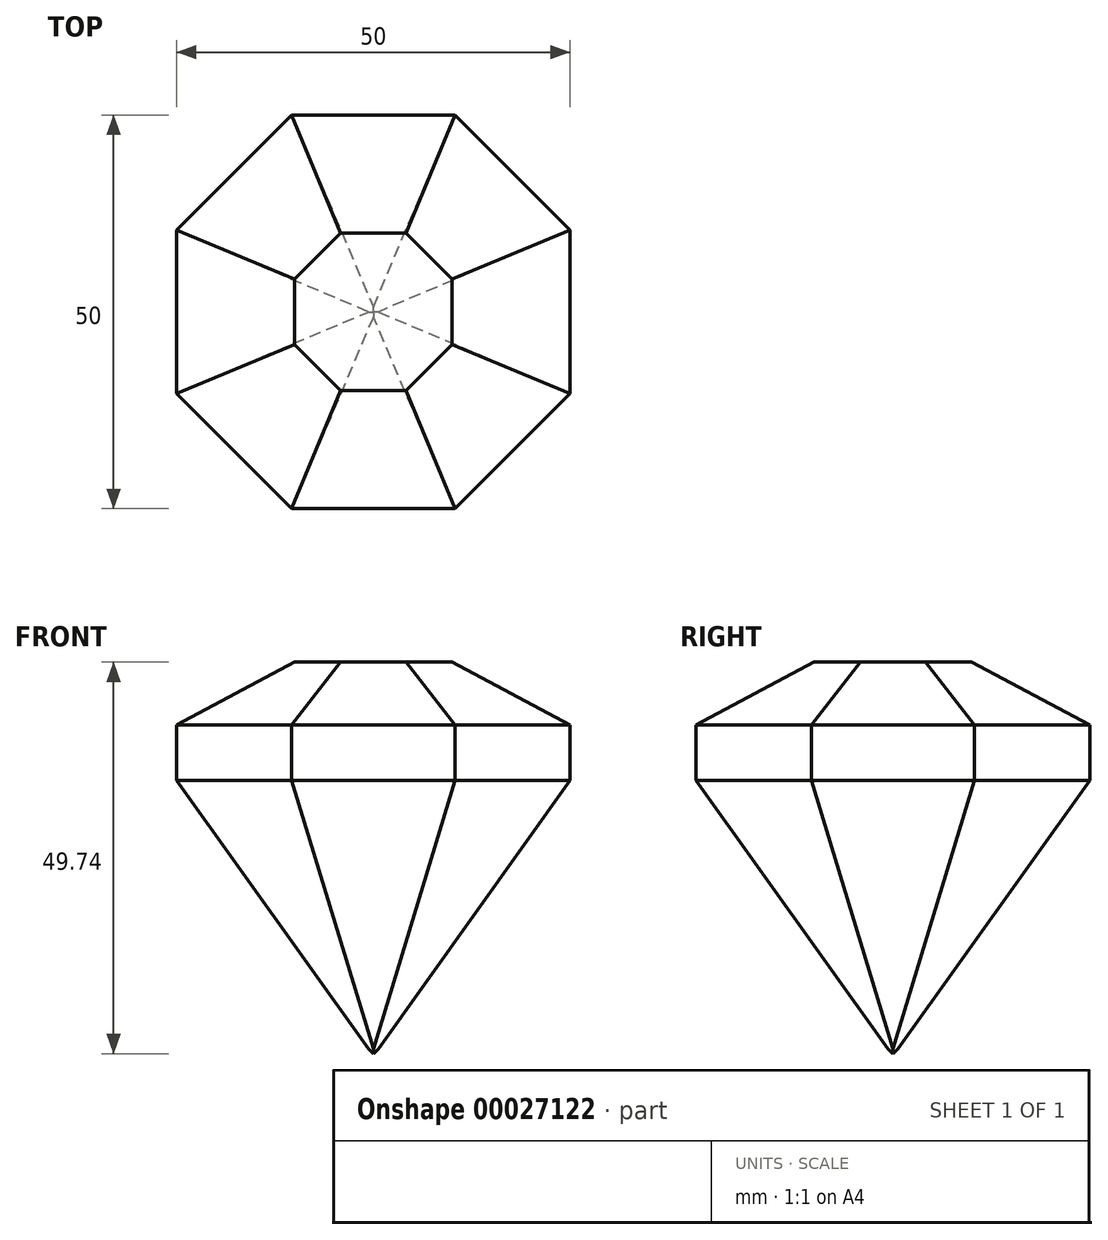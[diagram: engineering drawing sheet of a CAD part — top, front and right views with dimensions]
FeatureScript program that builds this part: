
annotation { "Feature Type Name" : "Feature", "Feature Type Description" : "" }
export const myFeature = defineFeature(function(context is Context, id is Id, definition is map)
    precondition{}
    {
        {
            var Q0;
            Q0=qCreatedBy(makeId("Front.planeOp"),FACE);
            var sketch = newSketch(context, id + "F0", { "sketchPlane" : qUnion([Q0])});
            skLineSegment(sketch, "E0.bottom", {"start": v(0, 0) * mm, "end": v(50, 0) * mm});
            skLineSegment(sketch, "E0.top", {"start": v(0, -50) * mm, "end": v(50, -50) * mm});
            skLineSegment(sketch, "E0.left", {"start": v(0, 0) * mm, "end": v(0, -50) * mm});
            skLineSegment(sketch, "E0.right", {"start": v(50, 0) * mm, "end": v(50, -50) * mm});
            skSolve(sketch);
        }
        {
            var Q0;
            Q0=makeQuery(id+"F0.imprint","IMPRINT",FACE,{"disambiguationData":[TD([[makeQuery(id+"F0.imprint","IMPRINT",EDGE,{"derivedFrom":sQuery(id+"F0.wireOp",EDGE,"E0.bottom")}),-1.0]])]});
            extrude(context, id + "F1", {"entities" : qUnion([Q0]), "depth" : 50 * mm});
        }
        {
            var Q0;
            Q0=makeQuery(id+"F1.opExtrude","CAP_EDGE",EDGE,{"disambiguationData":[OSD([sQuery(id+"F0.wireOp",EDGE,"E0.right")])],"isStart":false});
            cPlane(context, id + "F2", {"entities" : qUnion([Q0]), "cplaneType" : CPlaneType.LINE_ANGLE, "offset" : 150 * mm, "angle" : 45 * degree, "width" : 150 * mm, "height" : 150 * mm});
        }
        {
            var Q0;
            Q0=makeQuery(id+"F1.opExtrude","CAP_EDGE",EDGE,{"disambiguationData":[OSD([sQuery(id+"F0.wireOp",EDGE,"E0.left")])],"isStart":false});
            cPlane(context, id + "F3", {"entities" : qUnion([Q0]), "cplaneType" : CPlaneType.LINE_ANGLE, "offset" : 0 * mm, "angle" : 135 * degree, "width" : 150 * mm, "height" : 150 * mm});
        }
        {
            var Q0;
            Q0=makeQuery(id+"F1.opExtrude","CAP_FACE",FACE,{"disambiguationData":[OSD([sQuery(id+"F0.wireOp",EDGE,"E0.bottom"),sQuery(id+"F0.wireOp",EDGE,"E0.top"),sQuery(id+"F0.wireOp",EDGE,"E0.left"),sQuery(id+"F0.wireOp",EDGE,"E0.right")])],"isStart":false});
            var sketch = newSketch(context, id + "F4", { "sketchPlane" : qUnion([Q0])});
            skLineSegment(sketch, "E1", {"start": v(25, 0) * mm, "end": v(25, -50) * mm});
            skLineSegment(sketch, "E2", {"start": v(25, -50) * mm, "end": v(0, -15) * mm});
            skLineSegment(sketch, "E3", {"start": v(0, -15) * mm, "end": v(0, -8) * mm});
            skLineSegment(sketch, "E4", {"start": v(0, -8) * mm, "end": v(15, 0) * mm});
            skLineSegment(sketch, "E5", {"start": v(15, 0) * mm, "end": v(35, 0) * mm});
            skLineSegment(sketch, "E6", {"start": v(35, 0) * mm, "end": v(50, -8) * mm});
            skLineSegment(sketch, "E7", {"start": v(50, -8) * mm, "end": v(50, -15) * mm});
            skLineSegment(sketch, "E8", {"start": v(50, -15) * mm, "end": v(25, -50) * mm});
            skSolve(sketch);
        }
        {
            var Q0;
            {var subQ1=sQuery(id+"F4.wireOp",EDGE,"E4");Q0=makeQuery(id+"F4.imprint","IMPRINT",FACE,{"disambiguationData":[TD([[makeQuery(id+"F4.imprint","IMPRINT",EDGE,{"derivedFrom":subQ1}),1.0]])]});}
            var Q1;
            {var subQ1=sQuery(id+"F4.wireOp",EDGE,"E6");Q1=makeQuery(id+"F4.imprint","IMPRINT",FACE,{"disambiguationData":[TD([[makeQuery(id+"F4.imprint","IMPRINT",EDGE,{"derivedFrom":subQ1}),1.0]])]});}
            var Q2;
            {var subQ1=sQuery(id+"F4.wireOp",EDGE,"E8");Q2=makeQuery(id+"F4.imprint","IMPRINT",FACE,{"disambiguationData":[TD([[makeQuery(id+"F4.imprint","IMPRINT",EDGE,{"derivedFrom":subQ1}),1.0]])]});}
            var Q3;
            {var subQ1=sQuery(id+"F4.wireOp",EDGE,"E2");Q3=makeQuery(id+"F4.imprint","IMPRINT",FACE,{"disambiguationData":[TD([[makeQuery(id+"F4.imprint","IMPRINT",EDGE,{"derivedFrom":subQ1}),1.0]])]});}
            extrude(context, id + "F5", {"entities" : qUnion([Q0, Q1, Q2, Q3]), "operationType" : NewBodyOperationType.REMOVE, "endBound" : BoundingType.THROUGH_ALL, "oppositeDirection" : true, "depth" : 25 * mm});
        }
        {
            var Q0;
            Q0=makeQuery(id+"F1.opExtrude","SWEPT_FACE",FACE,{"disambiguationData":[OSD([sQuery(id+"F0.wireOp",EDGE,"E0.right")])]});
            var sketch = newSketch(context, id + "F6", { "sketchPlane" : qUnion([Q0])});
            skLineSegment(sketch, "E9", {"start": v(-25, 0) * mm, "end": v(-25, -50) * mm});
            skLineSegment(sketch, "E10", {"start": v(-25, -50) * mm, "end": v(-50, -15) * mm});
            skLineSegment(sketch, "E11", {"start": v(-50, -15) * mm, "end": v(-50, -8) * mm});
            skLineSegment(sketch, "E12", {"start": v(-50, -8) * mm, "end": v(-35, 0) * mm});
            skLineSegment(sketch, "E13", {"start": v(-35, 0) * mm, "end": v(-15, 0) * mm});
            skLineSegment(sketch, "E14", {"start": v(-15, 0) * mm, "end": v(0, -8) * mm});
            skLineSegment(sketch, "E15", {"start": v(0, -8) * mm, "end": v(0, -15) * mm});
            skLineSegment(sketch, "E16", {"start": v(0, -15) * mm, "end": v(-25, -50) * mm});
            skLineSegment(sketch, "E17.bottom", {"start": v(0, 0) * mm, "end": v(-50, 0) * mm});
            skLineSegment(sketch, "E17.top", {"start": v(0, -50) * mm, "end": v(-50, -50) * mm});
            skLineSegment(sketch, "E17.left", {"start": v(0, 0) * mm, "end": v(0, -50) * mm});
            skLineSegment(sketch, "E17.right", {"start": v(-50, 0) * mm, "end": v(-50, -50) * mm});
            skSolve(sketch);
        }
        {
            var Q0;
            {var subQ3=sQuery(id+"F6.wireOp",EDGE,"E12");Q0=makeQuery(id+"F6.imprint","IMPRINT",FACE,{"disambiguationData":[TD([[makeQuery(id+"F6.imprint","IMPRINT",EDGE,{"derivedFrom":subQ3}),1.0]])]});}
            var Q1;
            {var subQ3=sQuery(id+"F6.wireOp",EDGE,"E14");Q1=makeQuery(id+"F6.imprint","IMPRINT",FACE,{"disambiguationData":[TD([[makeQuery(id+"F6.imprint","IMPRINT",EDGE,{"derivedFrom":subQ3}),1.0]])]});}
            var Q2;
            {var subQ3=sQuery(id+"F6.wireOp",EDGE,"E16");Q2=makeQuery(id+"F6.imprint","IMPRINT",FACE,{"disambiguationData":[TD([[makeQuery(id+"F6.imprint","IMPRINT",EDGE,{"derivedFrom":subQ3}),1.0]])]});}
            var Q3;
            {var subQ3=sQuery(id+"F6.wireOp",EDGE,"E10");Q3=makeQuery(id+"F6.imprint","IMPRINT",FACE,{"disambiguationData":[TD([[makeQuery(id+"F6.imprint","IMPRINT",EDGE,{"derivedFrom":subQ3}),1.0]])]});}
            extrude(context, id + "F7", {"entities" : qUnion([Q0, Q1, Q2, Q3]), "operationType" : NewBodyOperationType.REMOVE, "endBound" : BoundingType.THROUGH_ALL, "oppositeDirection" : true, "depth" : 25 * mm});
        }
        {
            var Q0;
            Q0=qCreatedBy(id+"F2.planeOp",FACE);
            var sketch = newSketch(context, id + "F8", { "sketchPlane" : qUnion([Q0])});
            skLineSegment(sketch, "E18", {"start": v(0, 0.26) * mm, "end": v(0, -49.74) * mm});
            skLineSegment(sketch, "E19", {"start": v(0, -49.74) * mm, "end": v(-25, -15) * mm});
            skLineSegment(sketch, "E20", {"start": v(-25, -15) * mm, "end": v(-25, -8) * mm});
            skLineSegment(sketch, "E21", {"start": v(-25, -8) * mm, "end": v(-10, 0) * mm});
            skLineSegment(sketch, "E22", {"start": v(-10, 0) * mm, "end": v(10, 0) * mm});
            skLineSegment(sketch, "E23", {"start": v(10, 0) * mm, "end": v(25, -8) * mm});
            skLineSegment(sketch, "E24", {"start": v(25, -8) * mm, "end": v(25, -15) * mm});
            skLineSegment(sketch, "E25", {"start": v(25, -15) * mm, "end": v(0, -49.74) * mm});
            skLineSegment(sketch, "E26.bottom", {"start": v(25, 0) * mm, "end": v(-25, 0) * mm});
            skLineSegment(sketch, "E26.top", {"start": v(25, -50) * mm, "end": v(-25, -50) * mm});
            skLineSegment(sketch, "E26.left", {"start": v(25, 0) * mm, "end": v(25, -50) * mm});
            skLineSegment(sketch, "E26.right", {"start": v(-25, 0) * mm, "end": v(-25, -50) * mm});
            skLineSegment(sketch, "E27.bottom", {"start": v(42.72, 8.95) * mm, "end": v(-42.46, 8.95) * mm});
            skLineSegment(sketch, "E27.top", {"start": v(42.72, -61.04) * mm, "end": v(-42.46, -61.04) * mm});
            skLineSegment(sketch, "E27.left", {"start": v(42.72, 8.95) * mm, "end": v(42.72, -61.04) * mm});
            skLineSegment(sketch, "E27.right", {"start": v(-42.46, 8.95) * mm, "end": v(-42.46, -61.04) * mm});
            skSolve(sketch);
        }
        {
            var Q0;
            Q0 = qSketchRegion(id + "F8", true);
            var Q1;
            {var subQ0=sQuery(id+"F8.wireOp",EDGE,"E26.left");var subQ3=sQuery(id+"F8.wireOp",EDGE,"E23");var subQ4=makeQuery(id+"F8.imprint","INTERSECT",VERTEX,{"derivedFrom":[subQ3,subQ0]});Q1=makeQuery(id+"F8.imprint","IMPRINT",FACE,{"disambiguationData":[TD([[makeQuery(id+"F8.imprint","IMPRINT",EDGE,{"disambiguationData":[TD([[subQ4,1.0]])],"derivedFrom":subQ3}),1.0]])]});}
            var Q2;
            {var subQ2=sQuery(id+"F8.wireOp",EDGE,"E19");Q2=makeQuery(id+"F8.imprint","IMPRINT",FACE,{"disambiguationData":[TD([[makeQuery(id+"F8.imprint","IMPRINT",EDGE,{"derivedFrom":subQ2}),1.0]])]});}
            var Q3;
            {var subQ0=sQuery(id+"F8.wireOp",EDGE,"E26.right");var subQ3=sQuery(id+"F8.wireOp",EDGE,"E21");var subQ4=makeQuery(id+"F8.imprint","INTERSECT",VERTEX,{"derivedFrom":[subQ3,subQ0]});Q3=makeQuery(id+"F8.imprint","IMPRINT",FACE,{"disambiguationData":[TD([[makeQuery(id+"F8.imprint","IMPRINT",EDGE,{"disambiguationData":[TD([[subQ4,-1.0]])],"derivedFrom":subQ3}),1.0]])]});}
            extrude(context, id + "F9", {"entities" : qUnion([Q0, Q1, Q2, Q3]), "operationType" : NewBodyOperationType.REMOVE, "endBound" : BoundingType.THROUGH_ALL, "depth" : 25 * mm});
        }
        {
            var Q0;
            Q0=qCreatedBy(id+"F3.planeOp",FACE);
            var sketch = newSketch(context, id + "F10", { "sketchPlane" : qUnion([Q0])});
            skLineSegment(sketch, "E28", {"start": v(-35.36, 0) * mm, "end": v(-35.36, -49.74) * mm});
            skLineSegment(sketch, "E29", {"start": v(-35.36, -49.74) * mm, "end": v(-60.36, -15) * mm});
            skLineSegment(sketch, "E30", {"start": v(-60.36, -15) * mm, "end": v(-60.36, -8) * mm});
            skLineSegment(sketch, "E31", {"start": v(-60.36, -8) * mm, "end": v(-45.36, 0) * mm});
            skLineSegment(sketch, "E32", {"start": v(-45.36, 0) * mm, "end": v(-25.36, 0) * mm});
            skLineSegment(sketch, "E33", {"start": v(-25.36, 0) * mm, "end": v(-10.36, -8) * mm});
            skLineSegment(sketch, "E34", {"start": v(-10.36, -8) * mm, "end": v(-10.36, -15) * mm});
            skLineSegment(sketch, "E35", {"start": v(-10.36, -15) * mm, "end": v(-35.36, -49.74) * mm});
            skLineSegment(sketch, "E36.bottom", {"start": v(-10.36, 0) * mm, "end": v(-60.36, 0) * mm});
            skLineSegment(sketch, "E36.top", {"start": v(-10.36, -50) * mm, "end": v(-60.36, -50) * mm});
            skLineSegment(sketch, "E36.left", {"start": v(-10.36, 0) * mm, "end": v(-10.36, -50) * mm});
            skLineSegment(sketch, "E36.right", {"start": v(-60.36, 0) * mm, "end": v(-60.36, -50) * mm});
            skLineSegment(sketch, "E37.bottom", {"start": v(8.03, 16.62) * mm, "end": v(-77.15, 16.62) * mm});
            skLineSegment(sketch, "E37.top", {"start": v(8.03, -53.38) * mm, "end": v(-77.15, -53.38) * mm});
            skLineSegment(sketch, "E37.left", {"start": v(8.03, 16.62) * mm, "end": v(8.03, -53.38) * mm});
            skLineSegment(sketch, "E37.right", {"start": v(-77.15, 16.62) * mm, "end": v(-77.15, -53.38) * mm});
            skLineSegment(sketch, "E38", {"start": v(-31.22, 0) * mm, "end": v(-39.5, 0) * mm});
            skLineSegment(sketch, "E39", {"start": v(-21.21, 0) * mm, "end": v(0, -8) * mm});
            skSolve(sketch);
        }
        {
            var Q0;
            Q0 = qSketchRegion(id + "F10", true);
            var Q1;
            {var subQ3=sQuery(id+"F10.wireOp",EDGE,"E33");Q1=makeQuery(id+"F10.imprint","IMPRINT",FACE,{"disambiguationData":[TD([[makeQuery(id+"F10.imprint","IMPRINT",EDGE,{"derivedFrom":subQ3}),1.0]])]});}
            var Q2;
            {var subQ3=sQuery(id+"F10.wireOp",EDGE,"E31");Q2=makeQuery(id+"F10.imprint","IMPRINT",FACE,{"disambiguationData":[TD([[makeQuery(id+"F10.imprint","IMPRINT",EDGE,{"derivedFrom":subQ3}),1.0]])]});}
            var Q3;
            {var subQ2=sQuery(id+"F10.wireOp",EDGE,"E29");Q3=makeQuery(id+"F10.imprint","IMPRINT",FACE,{"disambiguationData":[TD([[makeQuery(id+"F10.imprint","IMPRINT",EDGE,{"derivedFrom":subQ2}),1.0]])]});}
            extrude(context, id + "F11", {"entities" : qUnion([Q0, Q1, Q2, Q3]), "operationType" : NewBodyOperationType.REMOVE, "endBound" : BoundingType.THROUGH_ALL, "depth" : 25 * mm});
        }
    });
